# Revit family: xWELED-WM_Wall Hosted_R16_V1.1
name_source: partatom
category: Lighting Fixtures
revit_build: Autodesk Revit 2016 (Build: 20150220_1215(x64)
units: mm (PartAtom-declared; Revit-internal decimal feet)

## family parameters
Always vertical = Yes
Cut with Voids When Loaded = No
Host = Wall
Light Source = Yes
OmniClass Number = 23.80.70.00
OmniClass Title = Lighting
Part Type = Normal
Room Calculation Point = No
Round Connector Dimension = Use Diameter
Shared = No

## types (10) — shared parameters
AS2293 Classification = C0=E1.25   C90=E1
Charger Method = Intelligent current limited constant voltage charger
Color Filter = 16777215
Construction = Polycarbonate (Base & Cover)
Dimensions = 130mm x 380mm x 190mm
Dimming Lamp Color Temperature Shift = <None>
Emit Shape Visible in Rendering = No
Emit from Rectangle Length = 1219 mm
Emit from Rectangle Width = 610 mm
IK Rating = IK08 (side surface), IK09 (front surface)
IP Rating = I66/67
Lamp = 6 x high intensity, low energy LED, 100,000hour
Mounting = Wall Mount
Operating Mode = Maintained
Operating Temperature = 0 to 40 C
Operating Voltage = 240V AC; 50Hz
Tilt Angle = 0.00°
Viewing Distance = 24M

## per-type parameters (varying)
| type | Battery type | Photometric Web File | Power Consumption | Product Description | Testing Mode |
| CWELED-WM-R | Lithium Iron Phosphate, 3.2V 1500mAh | ll18097 - CWELED-ZW-WM-RR.IES | 2.5W (standby)  5.1W (max) | LP Premium Wall Mount IP66/67 Weatherproof Exit, Enabled with Clevertest Plus | Clevertest Plus Enabled (not activated by default) |
| CWELED-DALI-WM-R | Lithium Iron Phosphate, 3.2V 1500mAh | ll18097 - CWELED-ZW-WM-RR.IES | 2.5W (standby)  5.1W (max) | LP Premium Wall Mount IP66/67 Weatherproof Exit | DALI Compatible |
| CWELED-DATA-WM-R | Lithium Iron Phosphate, 3.2V 1500mAh | ll18097 - CWELED-ZW-WM-RR.IES | 2.5W (standby)  5.1W (max) | LP Premium Wall Mount IP66/67 Weatherproof Exit | Zoneworks DATA |
| CWELED-ZW-WM-R | Lithium Iron Phosphate, 3.2V 1500mAh | ll18097 - CWELED-ZW-WM-RR.IES | 2.5W (standby)  5.1W (max) | LP Premium Wall Mount IP66/67 Weatherproof Exit | Zoneworks Computerised Testing |
| CWELED-CT-WM-R | Lithium Iron Phosphate, 3.2V 1500mAh | ll18097 - CWELED-ZW-WM-RR.IES | 2.5W (standby)  5.1W (max) | LP Premium Wall Mount IP66/67 Weatherproof Exit | Clevertest |
| LWELED-WM-R | Lithium Nanophosphate, 3.3V 2500mAh | ll16168 - LWELED.IES | 2.5W (standby)  4.8W (max) | L10 Optimum Wall Mount IP66/67 Weatherproof Exit, Enabled with Clevertest Plus | Clevertest Plus Enabled (not activated by default) |
| LWELED-CT-WM-R | Lithium Nanophosphate, 3.3V 2500mAh | ll16168 - LWELED.IES | 2.5W (standby)  4.8W (max) | L10 Optimum Wall Mount IP66/67 Weatherproof Exit | Clevertest |
| LWELED-DALI-WM-R | Lithium Nanophosphate, 3.3V 2500mAh | ll16168 - LWELED.IES | 2.5W (standby)  4.8W (max) | L10 Optimum Wall Mount IP66/67 Weatherproof Exit | DALI Compatible |
| LWELED-DATA-WM-R | Lithium Nanophosphate, 3.3V 2500mAh | ll16168 - LWELED.IES | 2.5W (standby)  4.8W (max) | L10 Optimum Wall Mount IP66/67 Weatherproof Exit | Zoneworks DATA COmputerised Testing System |
| LWELED-ZW-WM-R | Lithium Nanophosphate, 3.3V 2500mAh | ll16168 - LWELED.IES | 2.5W (standby)  4.8W (max) | L10 Optimum Wall Mount IP66/67 Weatherproof Exit | Zoneworks Computerised Testing |

## geometry (parser evidence)
native form markers: Sweep x2
no freeform markers — native parametric forms only
